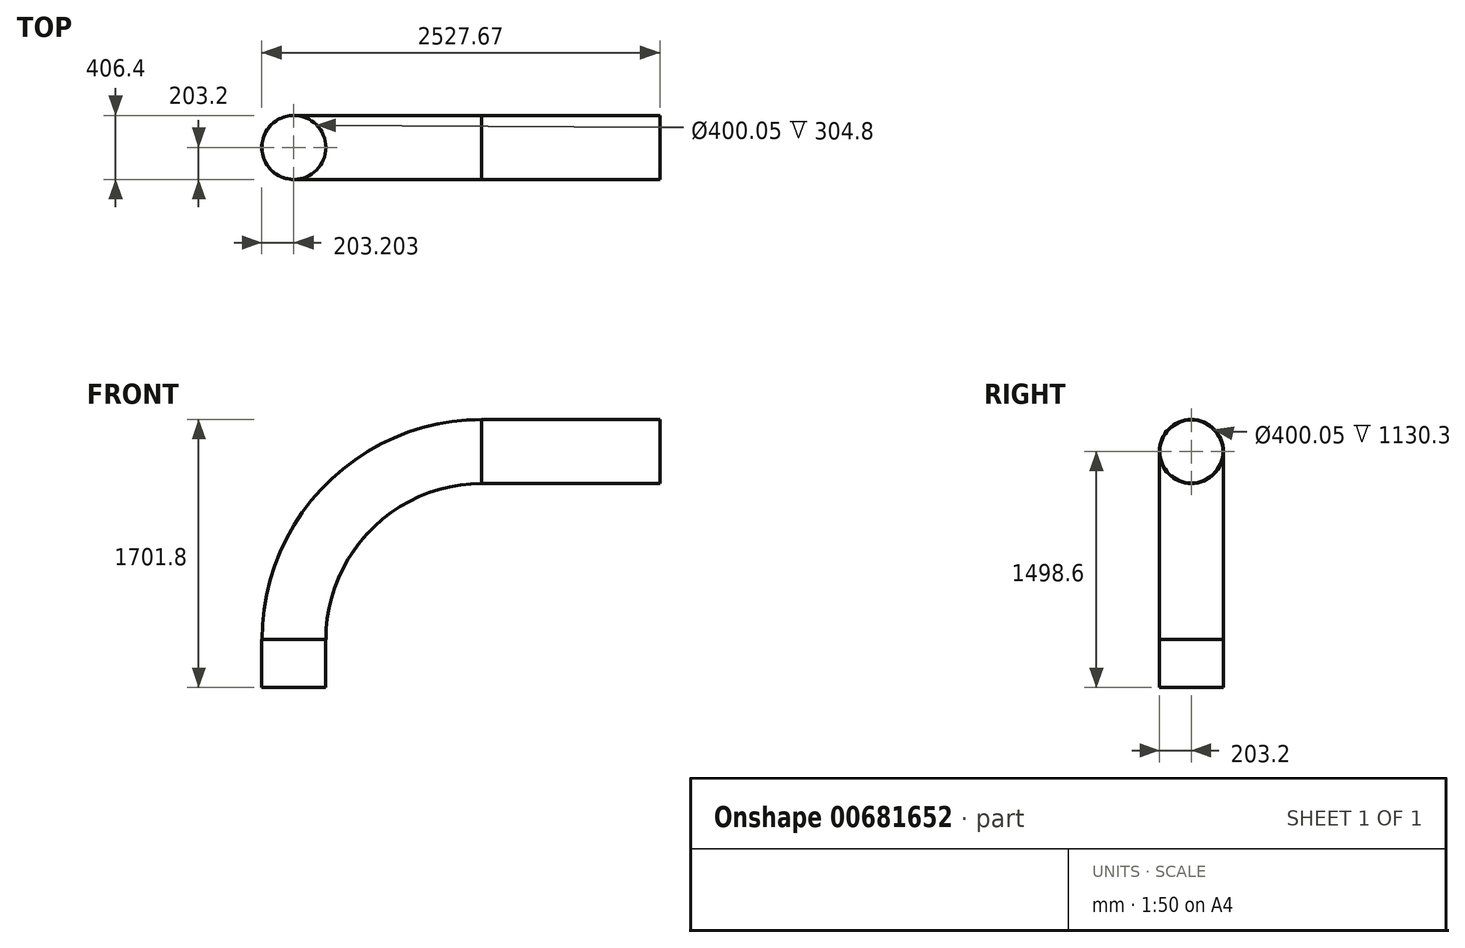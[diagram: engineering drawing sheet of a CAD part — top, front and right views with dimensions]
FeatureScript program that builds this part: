
annotation { "Feature Type Name" : "Feature", "Feature Type Description" : "" }
export const myFeature = defineFeature(function(context is Context, id is Id, definition is map)
    precondition{}
    {
        {
            var Q0;
            Q0=qCreatedBy(makeId("Front.planeOp"),FACE);
            var sketch = newSketch(context, id + "F0", { "sketchPlane" : qUnion([Q0])});
            skLineSegment(sketch, "E0", {"start": v(0, 0) * mm, "end": v(-88.9, 0) * mm, "construction": true});
            skLineSegment(sketch, "E1", {"start": v(-88.9, 0) * mm, "end": v(-1219.2, 0) * mm, "construction": true});
            skLineSegment(sketch, "E2", {"start": v(-1219.2, 0) * mm, "end": v(-2413, 0) * mm, "construction": true});
            skLineSegment(sketch, "E3", {"start": v(-2413, 0) * mm, "end": v(-2413, -1193.8) * mm, "construction": true});
            skLineSegment(sketch, "E4", {"start": v(-2413, -1193.8) * mm, "end": v(-2413, -1498.6) * mm, "construction": true});
            skLineSegment(sketch, "E5", {"start": v(-2413, -1498.6) * mm, "end": v(-2209.8, -1498.6) * mm, "construction": true});
            skLineSegment(sketch, "E6", {"start": v(0, 0) * mm, "end": v(0, -203.2) * mm, "construction": true});
            skLineSegment(sketch, "E7", {"start": v(-1219.2, 0) * mm, "end": v(-1219.2, -1193.8) * mm, "construction": true});
            skLineSegment(sketch, "E8", {"start": v(-1219.2, -1193.8) * mm, "end": v(-2413, -1193.8) * mm, "construction": true});
            skLineSegment(sketch, "E9", {"start": v(-88.9, 0) * mm, "end": v(-88.9, -203.2) * mm, "construction": true});
            skSolve(sketch);
        }
        {
            var Q0;
            Q0=sQuery(id+"F0.wireOp",EDGE,"E7");
            cPlane(context, id + "F1", {"entities" : qUnion([Q0]), "cplaneType" : CPlaneType.LINE_ANGLE, "offset" : 25.4 * mm, "angle" : 0 * degree, "width" : 152.4 * mm, "height" : 152.4 * mm});
        }
        {
            var Q0;
            Q0=sQuery(id+"F0.wireOp",EDGE,"E8");
            cPlane(context, id + "F2", {"entities" : qUnion([Q0]), "cplaneType" : CPlaneType.LINE_ANGLE, "offset" : 25.4 * mm, "angle" : 90 * degree, "width" : 152.4 * mm, "height" : 152.4 * mm});
        }
        {
            var Q0;
            Q0=sQuery(id+"F0.wireOp",EDGE,"E9");
            cPlane(context, id + "F3", {"entities" : qUnion([Q0]), "cplaneType" : CPlaneType.LINE_ANGLE, "offset" : 25.4 * mm, "angle" : 0 * degree, "width" : 152.4 * mm, "height" : 152.4 * mm});
        }
        {
            var Q0;
            Q0=qCreatedBy(id+"F3.planeOp",FACE);
            var sketch = newSketch(context, id + "F4", { "sketchPlane" : qUnion([Q0])});
            skCircle(sketch, "E10", {"center": v(0, 0) * mm, "radius": 203.2 * mm});
            skCircle(sketch, "E11", {"center": v(0, 0) * mm, "radius": 200.03 * mm});
            skSolve(sketch);
        }
        {
            var Q0;
            Q0 = qSketchRegion(id + "F4", true);
            extrude(context, id + "F5", {"entities" : qUnion([Q0]), "depth" : 1130.3 * mm, "offsetDistance" : 25.4 * mm});
        }
        {
            var Q0;
            Q0=qCreatedBy(id+"F1.planeOp",FACE);
            var sketch = newSketch(context, id + "F6", { "sketchPlane" : qUnion([Q0])});
            skLineSegment(sketch, "E12", {"start": v(0, -1193.8) * mm, "end": v(203.2, -1193.8) * mm, "construction": true});
            skCircle(sketch, "E13", {"center": v(0, 0) * mm, "radius": 203.2 * mm});
            skCircle(sketch, "E14", {"center": v(0, 0) * mm, "radius": 200.03 * mm});
            skSolve(sketch);
        }
        {
            var Q0;
            Q0=makeQuery(id+"F6.imprint","IMPRINT",FACE,{"disambiguationData":[TD([[makeQuery(id+"F6.imprint","IMPRINT",EDGE,{"derivedFrom":sQuery(id+"F6.wireOp",EDGE,"E14")}),1.0]])]});
            var Q1;
            Q1=sQuery(id+"F6.wireOp",EDGE,"E12");
            revolve(context, id + "F7", {"surfaceOperationType" : NewSurfaceOperationType.NEW, "entities" : qUnion([Q0]), "axis" : qUnion([Q1]), "revolveType" : RevolveType.ONE_DIRECTION, "angle" : 90 * degree});
        }
        {
            var Q0;
            Q0=qCreatedBy(id+"F2.planeOp",FACE);
            var sketch = newSketch(context, id + "F8", { "sketchPlane" : qUnion([Q0])});
            skCircle(sketch, "E15", {"center": v(-2413.37, 0) * mm, "radius": 203.2 * mm});
            skCircle(sketch, "E16", {"center": v(-2413.37, 0) * mm, "radius": 200.03 * mm});
            skSolve(sketch);
        }
        {
            var Q0;
            Q0=makeQuery(id+"F7.opRevolve","CAP_FACE",FACE,{"disambiguationData":[OSD([sQuery(id+"F6.wireOp",EDGE,"E14")])],"isStart":false});
            extrude(context, id + "F9", {"entities" : qUnion([Q0]), "depth" : 304.8 * mm, "offsetDistance" : 25.4 * mm});
        }
        {
            var Q0;
            Q0=makeQuery(id+"F7.opRevolve","SWEPT_BODY",BODY,{"disambiguationData":[OSD([sQuery(id+"F6.wireOp",EDGE,"E14")])]});
            deleteBodies(context, id + "F10", {"entities" : qUnion([Q0])});
        }
        {
            var Q0;
            Q0=makeQuery(id+"F6.imprint","IMPRINT",FACE,{"disambiguationData":[TD([[makeQuery(id+"F6.imprint","IMPRINT",EDGE,{"derivedFrom":sQuery(id+"F6.wireOp",EDGE,"E13")}),1.0]])]});
            var Q1;
            Q1=sQuery(id+"F6.wireOp",EDGE,"E12");
            revolve(context, id + "F11", {"surfaceOperationType" : NewSurfaceOperationType.NEW, "entities" : qUnion([Q0]), "axis" : qUnion([Q1]), "revolveType" : RevolveType.ONE_DIRECTION, "angle" : 90 * degree});
        }
        {
            var Q0;
            Q0=makeQuery(id+"F9.opExtrude","SWEPT_BODY",BODY,{"disambiguationData":[OSD([sQuery(id+"F6.wireOp",EDGE,"E14")])]});
            deleteBodies(context, id + "F12", {"entities" : qUnion([Q0])});
        }
        {
            var Q0;
            Q0=makeQuery(id+"F8.imprint","IMPRINT",FACE,{"disambiguationData":[TD([[makeQuery(id+"F8.imprint","IMPRINT",EDGE,{"derivedFrom":sQuery(id+"F8.wireOp",EDGE,"E15")}),1.0]])]});
            var Q1;
            Q1=sQuery(id+"F8.wireOp",EDGE,"E15");
            var Q2;
            Q2=sQuery(id+"F8.wireOp",EDGE,"E16");
            extrude(context, id + "F13", {"entities" : qUnion([Q0]), "surfaceEntities" : qUnion([Q1, Q2]), "oppositeDirection" : true, "depth" : 304.8 * mm, "offsetDistance" : 25.4 * mm});
        }
    });
